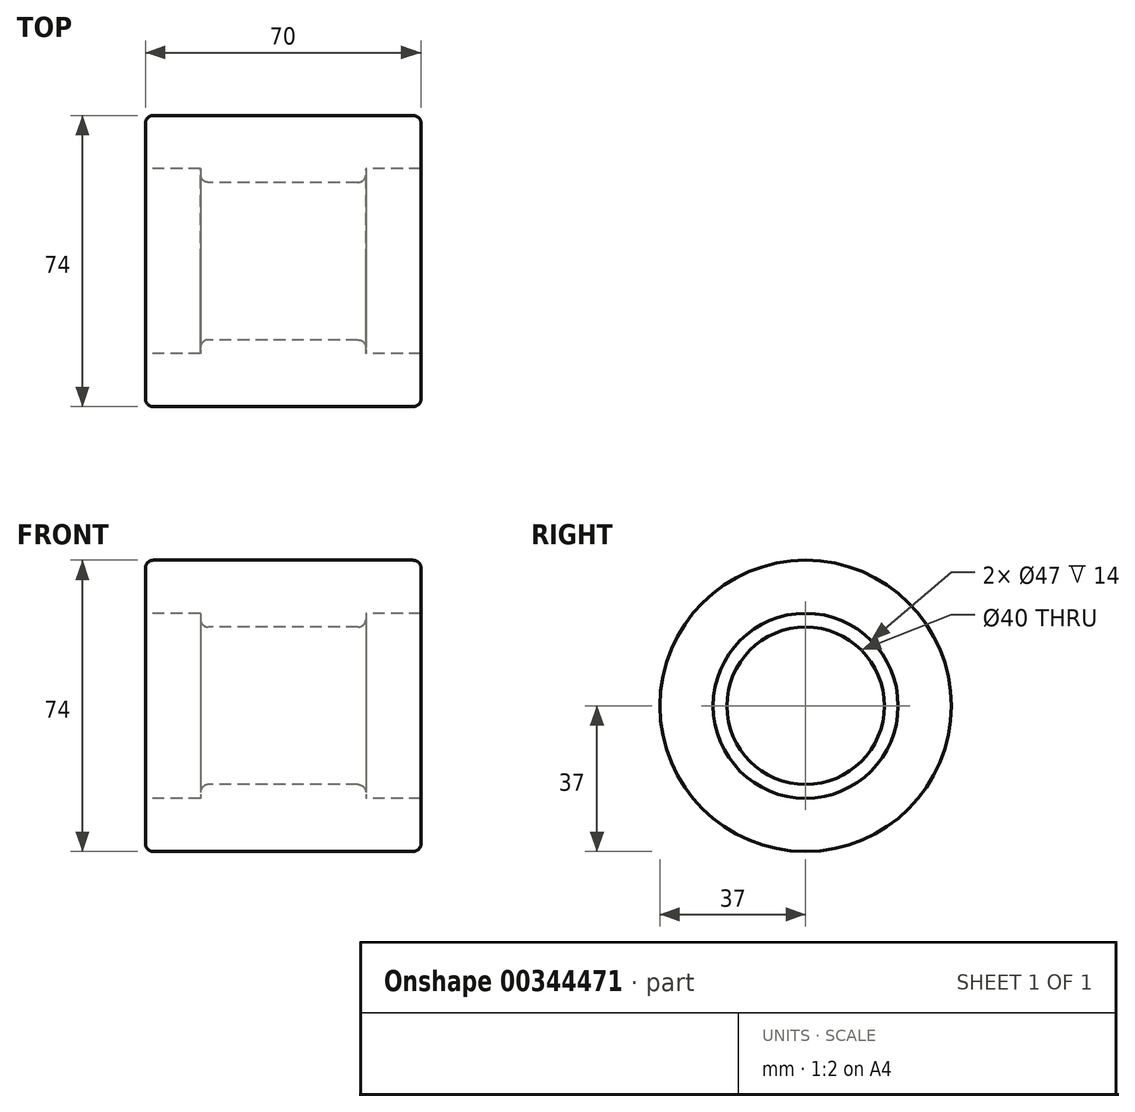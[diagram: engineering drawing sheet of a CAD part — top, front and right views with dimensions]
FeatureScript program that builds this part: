
annotation { "Feature Type Name" : "Feature", "Feature Type Description" : "" }
export const myFeature = defineFeature(function(context is Context, id is Id, definition is map)
    precondition{}
    {
        {
            var Q0;
            Q0=qCreatedBy(makeId("Right.planeOp"),FACE);
            var sketch = newSketch(context, id + "F0", { "sketchPlane" : qUnion([Q0])});
            skCircle(sketch, "E0", {"center": v(0, 0) * mm, "radius": 37 * mm});
            skSolve(sketch);
        }
        {
            var Q0;
            Q0 = qSketchRegion(id + "F0", true);
            extrude(context, id + "F1", {"entities" : qUnion([Q0]), "endBound" : BoundingType.SYMMETRIC, "depth" : 70 * mm});
        }
        {
            var Q0;
            Q0=qCreatedBy(makeId("Front.planeOp"),FACE);
            var sketch = newSketch(context, id + "F2", { "sketchPlane" : qUnion([Q0])});
            skLineSegment(sketch, "E1", {"start": v(0, 20) * mm, "end": v(21, 20) * mm});
            skLineSegment(sketch, "E2", {"start": v(21, 20) * mm, "end": v(21, 23.5) * mm});
            skLineSegment(sketch, "E3", {"start": v(21, 23.5) * mm, "end": v(35, 23.5) * mm});
            skLineSegment(sketch, "E4", {"start": v(35, 23.5) * mm, "end": v(35, 0) * mm});
            skLineSegment(sketch, "E5", {"start": v(35, 0) * mm, "end": v(0, 0) * mm});
            skLineSegment(sketch, "E6", {"start": v(0, 0) * mm, "end": v(0, 20) * mm, "construction": true});
            skLineSegment(sketch, "E7.MirrorCS", {"start": v(-35, 0) * mm, "end": v(0, 0) * mm});
            skLineSegment(sketch, "E8.MirrorCS", {"start": v(-35, 23.5) * mm, "end": v(-35, 0) * mm});
            skLineSegment(sketch, "E9.MirrorCS", {"start": v(-21, 23.5) * mm, "end": v(-35, 23.5) * mm});
            skLineSegment(sketch, "E10.MirrorCS", {"start": v(0, 20) * mm, "end": v(-21, 20) * mm});
            skLineSegment(sketch, "E11.MirrorCS", {"start": v(-21, 20) * mm, "end": v(-21, 23.5) * mm});
            skSolve(sketch);
        }
        {
            var Q0;
            Q0 = qSketchRegion(id + "F2", true);
            var Q1;
            Q1=sQuery(id+"F2.wireOp",EDGE,"E5");
            revolve(context, id + "F3", {"operationType" : NewBodyOperationType.REMOVE, "entities" : qUnion([Q0]), "axis" : qUnion([Q1]), "revolveType" : RevolveType.FULL, "oppositeDirection" : true});
        }
        {
            var Q0;
            Q0=makeQuery(id+"F1.opExtrude","SWEPT_FACE",FACE,{"disambiguationData":[OSD([sQuery(id+"F0.wireOp",EDGE,"E0")])]});
            var Q1;
            Q1=makeQuery(id+"F3.boolean.opBoolean","COPY",EDGE,{"derivedFrom":makeQuery(id+"F3.opRevolve","SWEPT_EDGE",EDGE,{"disambiguationData":[OSD([sQuery(id+"F2.wireOp",EDGE,"E3"),sQuery(id+"F2.wireOp",EDGE,"E4")])]})});
            var Q2;
            Q2=makeQuery(id+"F3.boolean.opBoolean","COPY",EDGE,{"derivedFrom":makeQuery(id+"F3.opRevolve","SWEPT_EDGE",EDGE,{"disambiguationData":[OSD([sQuery(id+"F2.wireOp",EDGE,"E8.MirrorCS"),sQuery(id+"F2.wireOp",EDGE,"E9.MirrorCS")])]})});
            var Q3;
            Q3=makeQuery(id+"F3.boolean.opBoolean","COPY",EDGE,{"derivedFrom":makeQuery(id+"F3.opRevolve","SWEPT_EDGE",EDGE,{"disambiguationData":[OSD([sQuery(id+"F2.wireOp",EDGE,"E10.MirrorCS"),sQuery(id+"F2.wireOp",EDGE,"E11.MirrorCS")])]})});
            var Q4;
            Q4=makeQuery(id+"F3.boolean.opBoolean","COPY",EDGE,{"derivedFrom":makeQuery(id+"F3.opRevolve","SWEPT_EDGE",EDGE,{"disambiguationData":[OSD([sQuery(id+"F2.wireOp",EDGE,"E1"),sQuery(id+"F2.wireOp",EDGE,"E2")])]})});
            fillet(context, id + "F4", {"entities" : qUnion([Q0, Q1, Q2, Q3, Q4]), "radius" : 2 * mm, "tangentPropagation" : true, "allowEdgeOverflow" : false});
        }
    });
